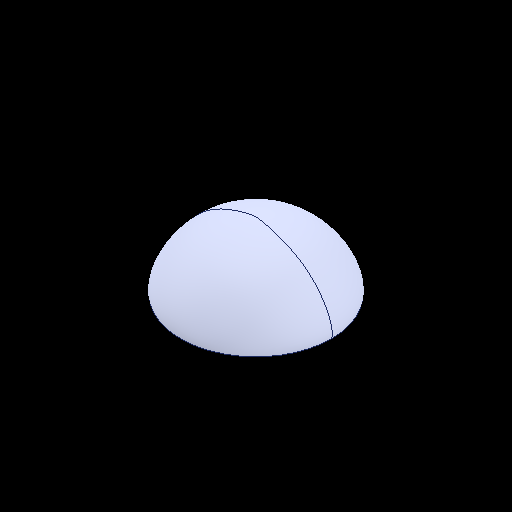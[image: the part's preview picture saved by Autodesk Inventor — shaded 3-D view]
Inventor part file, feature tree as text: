
AUTODESK INVENTOR PART (.ipt)
format: ipt  version: 2023 (Build 270158000, 158)  size: 122,368 bytes
history: native  units: in
note: dims shown in document units (in); Inventor stores cm internally (conversion verified against a paired STEP export)
features: revolve x1
ambient origin geometry x8: Origin, YZ Plane, XZ Plane, XY Plane, X Axis, Y Axis, Z Axis, Center Point
bodies: Solid1 (feature_tree)
feature tree (1):
  revolve  "Revolve1"  [1 undecoded]
note: 1 required parameter value undecoded (feature->parameter linkage not recoverable at this tier; creation-order binding heuristic only, values carry confidence <= 0.55)
